# Revit family: PLCD
name_source: partatom
category: Mechanical Equipment
units: mm (PartAtom-declared; Revit-internal decimal feet)

## family parameters
Always vertical = Yes
Cut with Voids When Loaded = No
Part Type = Normal
Room Calculation Point = No
Round Connector Dimension = Use Diameter
Shared = No
Work Plane-Based = No

## types (20) — shared parameters
0 = 0' - 0"
1" = 0' - 1"
1.125" = 0' - 1 1/8"
1.5 = 0' - 1 1/2"
2" = 0' - 2"
2' = 2' - 0"
3" = 0' - 3"
4" = 0' - 4"
45 = 50.00°
FORMULA_A = 0' - 0"
FORMULA_K = 0' - 0"
Manufacturer = Loren Cook Company
Model = PLCD
ONE EIGTH = 0' - 0 1/8"
PERCENT_WIDE = 100
Type Comments = Centrifugal Plenum Fan Direct Drive Arr 4 Class 1-3
URL = www.lorencook.com
zero-valued in all types: PERCENT_A

## per-type parameters (varying)
- 120_PLCD: (C-H-H-H-H)/2=0' - 7 3/16"; (E/2)-.125"=0' - 1 11/32"; -(C - H - H - H - H) / 2=-0' - 7 3/16"; 2H=0' - 1 7/16"; A=2' - 2 5/16"; A-K-L-.125"-H-H=1' - 1 1/2"; A-L=2' - 0 1/2"; B=1' - 5 1/4"; B-E=1' - 2 5/16"; B/2=0' - 8 5/8"; C=1' - 5 1/4"; C/2=0' - 8 5/8"; D=0' - 8 5/8"; D-MOTOR_RADIUS-2"=0' - 3 5/8"; E=0' - 2 15/16"; E/2=0' - 1 15/32"; F=0' - 0 5/8"; F/2=0' - 0 5/16"; FORMULA2_A=2' - 2 5/16"; FORMULA2_K=0' - 9 7/16"; H=0' - 0 23/32"; INLET_DEPTH=0' - 3 25/32"; INLET_RAD=0' - 6 29/32"; J=1' - 4 1/4"; J-2"=-1' - 0 13/16"; K=0' - 9 7/16"; L=0' - 1 13/16"; L+K=0' - 11 1/4"; L+K+.125"=0' - 11 3/8"; L-.125"=0' - 1 11/16"; MOTOR_RADIUS=0' - 3"; MOTOR_RADIUS+1.5"=0' - 5"; MOTOR_RADIUS+2"=0' - 5"; UNIT_SIZE=120
- 135_PLCD: (C-H-H-H-H)/2=0' - 8 5/16"; (E/2)-.125"=0' - 1 15/32"; -(C - H - H - H - H) / 2=-0' - 8 5/16"; 2H=0' - 1 7/16"; A=2' - 3 5/32"; A-K-L-.125"-H-H=1' - 1 1/32"; A-L=2' - 1 3/32"; B=1' - 7 1/2"; B-E=1' - 4 5/16"; B/2=0' - 9 3/4"; C=1' - 7 1/2"; C/2=0' - 9 3/4"; D=0' - 9 3/4"; D-MOTOR_RADIUS-2"=0' - 5 3/4"; E=0' - 3 3/16"; E/2=0' - 1 19/32"; F=0' - 0 5/8"; F/2=0' - 0 5/16"; FORMULA2_A=2' - 3 5/32"; FORMULA2_K=0' - 10 1/2"; H=0' - 0 23/32"; INLET_DEPTH=0' - 4 3/16"; INLET_RAD=0' - 7 13/16"; J=1' - 3 3/4"; J-2"=-1' - 0 5/16"; K=0' - 10 1/2"; L=0' - 2 1/16"; L+K=1' - 0 9/16"; L+K+.125"=1' - 0 11/16"; L-.125"=0' - 1 15/16"; MOTOR_RADIUS=0' - 2"; MOTOR_RADIUS+1.5"=0' - 4"; MOTOR_RADIUS+2"=0' - 4"; UNIT_SIZE=135
- 150_PLCD: (C-H-H-H-H)/2=0' - 9 5/16"; (E/2)-.125"=0' - 1 15/32"; -(C - H - H - H - H) / 2=-0' - 9 5/16"; 2H=0' - 1 7/16"; A=2' - 5 27/32"; A-K-L-.125"-H-H=1' - 2 25/32"; A-L=2' - 3 25/32"; B=1' - 9 1/2"; B-E=1' - 6 5/16"; B/2=0' - 10 3/4"; C=1' - 9 1/2"; C/2=0' - 10 3/4"; D=0' - 10 3/4"; D-MOTOR_RADIUS-2"=0' - 5 1/4"; E=0' - 3 3/16"; E/2=0' - 1 19/32"; F=0' - 0 5/8"; F/2=0' - 0 5/16"; FORMULA2_A=2' - 5 27/32"; FORMULA2_K=0' - 11 7/16"; H=0' - 0 23/32"; INLET_DEPTH=0' - 4 9/16"; INLET_RAD=0' - 8 19/32"; J=1' - 5 1/2"; J-2"=-1' - 2 1/16"; K=0' - 11 7/16"; L=0' - 2 1/16"; L+K=1' - 1 1/2"; L+K+.125"=1' - 1 5/8"; L-.125"=0' - 1 15/16"; MOTOR_RADIUS=0' - 3 1/2"; MOTOR_RADIUS+1.5"=0' - 5 1/2"; MOTOR_RADIUS+2"=0' - 5 1/2"; UNIT_SIZE=150
- 165_PLCD: (C-H-H-H-H)/2=0' - 10 7/16"; (E/2)-.125"=0' - 1 15/32"; -(C - H - H - H - H) / 2=-0' - 10 7/16"; 2H=0' - 1 7/16"; A=2' - 8 7/16"; A-K-L-.125"-H-H=1' - 4 3/16"; A-L=2' - 6 3/8"; B=1' - 11 3/4"; B-E=1' - 8 9/16"; B/2=0' - 11 7/8"; C=1' - 11 3/4"; C/2=0' - 11 7/8"; D=0' - 11 7/8"; D-MOTOR_RADIUS-2"=0' - 5 7/8"; E=0' - 3 3/16"; E/2=0' - 1 19/32"; F=0' - 0 5/8"; F/2=0' - 0 5/16"; FORMULA2_A=2' - 8 7/16"; FORMULA2_K=1' - 0 5/8"; H=0' - 0 23/32"; INLET_DEPTH=0' - 5 1/16"; INLET_RAD=0' - 9 1/2"; J=1' - 6 7/8"; J-2"=-1' - 3 7/16"; K=1' - 0 5/8"; L=0' - 2 1/16"; L+K=1' - 2 11/16"; L+K+.125"=1' - 2 13/16"; L-.125"=0' - 1 15/16"; MOTOR_RADIUS=0' - 4"; MOTOR_RADIUS+1.5"=0' - 6"; MOTOR_RADIUS+2"=0' - 6"; UNIT_SIZE=165
- 180_PLCD: (C-H-H-H-H)/2=0' - 11 7/16"; (E/2)-.125"=0' - 1 31/32"; -(C - H - H - H - H) / 2=-0' - 11 7/16"; 2H=0' - 1 7/16"; A=2' - 10 17/32"; A-K-L-.125"-H-H=1' - 4 5/32"; A-L=2' - 7 15/32"; B=2' - 1 3/4"; B-E=1' - 9 9/16"; B/2=1' - 0 7/8"; C=2' - 1 3/4"; C/2=1' - 0 7/8"; D=1' - 0 7/8"; D-MOTOR_RADIUS-2"=0' - 6 7/8"; E=0' - 4 3/16"; E/2=0' - 2 3/32"; F=0' - 0 5/8"; F/2=0' - 0 5/16"; FORMULA2_A=2' - 10 17/32"; FORMULA2_K=1' - 1 3/4"; H=0' - 0 23/32"; INLET_DEPTH=0' - 5 1/2"; INLET_RAD=0' - 10 5/16"; J=1' - 6 7/8"; J-2"=-1' - 3 7/16"; K=1' - 1 3/4"; L=0' - 3 1/16"; L+K=1' - 4 13/16"; L+K+.125"=1' - 4 15/16"; L-.125"=0' - 2 15/16"; MOTOR_RADIUS=0' - 4"; MOTOR_RADIUS+1.5"=0' - 6"; MOTOR_RADIUS+2"=0' - 6"; UNIT_SIZE=180
- 195_PLCD: (C-H-H-H-H)/2=1' - 0 9/16"; (E/2)-.125"=0' - 1 31/32"; -(C - H - H - H - H) / 2=-1' - 0 9/16"; 2H=0' - 1 7/16"; A=2' - 11 21/32"; A-K-L-.125"-H-H=1' - 4 5/32"; A-L=2' - 8 19/32"; B=2' - 4"; B-E=1' - 11 13/16"; B/2=1' - 2"; C=2' - 4"; C/2=1' - 2"; D=1' - 2"; D-MOTOR_RADIUS-2"=0' - 8"; E=0' - 4 3/16"; E/2=0' - 2 3/32"; F=0' - 0 5/8"; F/2=0' - 0 5/16"; FORMULA2_A=2' - 11 21/32"; FORMULA2_K=1' - 2 7/8"; H=0' - 0 23/32"; INLET_DEPTH=0' - 5 15/16"; INLET_RAD=0' - 11 3/16"; J=1' - 6 7/8"; J-2"=-1' - 3 7/16"; K=1' - 2 7/8"; L=0' - 3 1/16"; L+K=1' - 5 15/16"; L+K+.125"=1' - 6 1/16"; L-.125"=0' - 2 15/16"; MOTOR_RADIUS=0' - 4"; MOTOR_RADIUS+1.5"=0' - 6"; MOTOR_RADIUS+2"=0' - 6"; UNIT_SIZE=195
- 210_PLCD: (C-H-H-H-H)/2=1' - 1 9/16"; (E/2)-.125"=0' - 1 31/32"; -(C - H - H - H - H) / 2=-1' - 1 9/16"; 2H=0' - 1 7/16"; A=3' - 4 3/8"; A-K-L-.125"-H-H=1' - 7 13/16"; A-L=3' - 1 5/16"; B=2' - 6"; B-E=2' - 1 13/16"; B/2=1' - 3"; C=2' - 6"; C/2=1' - 3"; D=1' - 3"; D-MOTOR_RADIUS-2"=0' - 7 13/16"; E=0' - 4 3/16"; E/2=0' - 2 3/32"; F=0' - 0 5/8"; F/2=0' - 0 5/16"; FORMULA2_A=3' - 4 3/8"; FORMULA2_K=1' - 3 15/16"; H=0' - 0 23/32"; INLET_DEPTH=0' - 6 3/8"; INLET_RAD=1' - 0"; J=1' - 10 1/2"; J-2"=-1' - 7 1/16"; K=1' - 3 15/16"; L=0' - 3 1/16"; L+K=1' - 7"; L+K+.125"=1' - 7 1/8"; L-.125"=0' - 2 15/16"; MOTOR_RADIUS=0' - 5 3/16"; MOTOR_RADIUS+1.5"=0' - 7 3/16"; MOTOR_RADIUS+2"=0' - 7 3/16"; UNIT_SIZE=210
- 225_PLCD: (C-H-H-H-H)/2=1' - 2 11/16"; (E/2)-.125"=0' - 1 31/32"; -(C - H - H - H - H) / 2=-1' - 2 11/16"; 2H=0' - 1 7/16"; A=3' - 5 3/8"; A-K-L-.125"-H-H=1' - 7 13/16"; A-L=3' - 2 5/16"; B=2' - 8 1/4"; B-E=2' - 4 1/16"; B/2=1' - 4 1/8"; C=2' - 8 1/4"; C/2=1' - 4 1/8"; D=1' - 4 1/8"; D-MOTOR_RADIUS-2"=0' - 8 15/16"; E=0' - 4 3/16"; E/2=0' - 2 3/32"; F=0' - 0 5/8"; F/2=0' - 0 5/16"; FORMULA2_A=3' - 5 3/8"; FORMULA2_K=1' - 4 15/16"; H=0' - 0 23/32"; INLET_DEPTH=0' - 6 25/32"; INLET_RAD=1' - 0 29/32"; J=1' - 10 1/2"; J-2"=-1' - 7 1/16"; K=1' - 4 15/16"; L=0' - 3 1/16"; L+K=1' - 8"; L+K+.125"=1' - 8 1/8"; L-.125"=0' - 2 15/16"; MOTOR_RADIUS=0' - 5 3/16"; MOTOR_RADIUS+1.5"=0' - 7 3/16"; MOTOR_RADIUS+2"=0' - 7 3/16"; UNIT_SIZE=225
- 245_PLCD: (C-H-H-H-H)/2=1' - 4 1/16"; (E/2)-.125"=0' - 1 31/32"; -(C - H - H - H - H) / 2=-1' - 4 1/16"; 2H=0' - 1 7/16"; A=4' - 0 1/8"; A-K-L-.125"-H-H=2' - 1 1/8"; A-L=3' - 9 1/16"; B=2' - 11"; B-E=2' - 6 13/16"; B/2=1' - 5 1/2"; C=2' - 11"; C/2=1' - 5 1/2"; D=1' - 5 1/2"; D-MOTOR_RADIUS-2"=0' - 9 3/16"; E=0' - 4 3/16"; E/2=0' - 2 3/32"; F=0' - 0 5/8"; F/2=0' - 0 5/16"; FORMULA2_A=4' - 0 1/8"; FORMULA2_K=1' - 6 3/8"; H=0' - 0 23/32"; INLET_DEPTH=0' - 7 11/32"; INLET_RAD=1' - 2"; J=2' - 3 3/4"; J-2"=-2' - 0 5/16"; K=1' - 6 3/8"; L=0' - 3 1/16"; L+K=1' - 9 7/16"; L+K+.125"=1' - 9 9/16"; L-.125"=0' - 2 15/16"; MOTOR_RADIUS=0' - 6 5/16"; MOTOR_RADIUS+1.5"=0' - 8 5/16"; MOTOR_RADIUS+2"=0' - 8 5/16"; UNIT_SIZE=245
- 270_PLCD: (C-H-H-H-H)/2=1' - 5 15/16"; (E/2)-.125"=0' - 2 7/32"; -(C - H - H - H - H) / 2=-1' - 5 15/16"; 2H=0' - 1 7/16"; A=4' - 5 5/16"; A-K-L-.125"-H-H=2' - 3 7/8"; A-L=4' - 1 3/4"; B=3' - 2 3/4"; B-E=2' - 10 1/16"; B/2=1' - 7 3/8"; C=3' - 2 3/4"; C/2=1' - 7 3/8"; D=1' - 7 3/8"; D-MOTOR_RADIUS-2"=0' - 11 1/16"; E=0' - 4 11/16"; E/2=0' - 2 11/32"; F=0' - 0 5/8"; F/2=0' - 0 5/16"; FORMULA2_A=4' - 5 5/16"; FORMULA2_K=1' - 8 5/16"; H=0' - 0 23/32"; INLET_DEPTH=0' - 8 1/8"; INLET_RAD=1' - 3 1/2"; J=2' - 6 5/8"; J-2"=-2' - 3 3/16"; K=1' - 8 5/16"; L=0' - 3 9/16"; L+K=1' - 11 7/8"; L+K+.125"=2' - 0"; L-.125"=0' - 3 7/16"; MOTOR_RADIUS=0' - 6 5/16"; MOTOR_RADIUS+1.5"=0' - 8 5/16"; MOTOR_RADIUS+2"=0' - 8 5/16"; UNIT_SIZE=270
- 300_PLCD: (C-H-H-H-H)/2=1' - 8 1/16"; (E/2)-.125"=0' - 2 7/32"; -(C - H - H - H - H) / 2=-1' - 8 1/16"; 2H=0' - 1 7/16"; A=4' - 10 13/32"; A-K-L-.125"-H-H=2' - 6 29/32"; A-L=4' - 6 27/32"; B=3' - 7"; B-E=3' - 2 5/16"; B/2=1' - 9 1/2"; C=3' - 7"; C/2=1' - 9 1/2"; D=1' - 9 1/2"; D-MOTOR_RADIUS-2"=0' - 11 11/16"; E=0' - 4 11/16"; E/2=0' - 2 11/32"; F=0' - 0 5/8"; F/2=0' - 0 5/16"; FORMULA2_A=4' - 10 13/32"; FORMULA2_K=1' - 10 3/8"; H=0' - 0 23/32"; INLET_DEPTH=0' - 8 15/16"; INLET_RAD=1' - 5 3/16"; J=2' - 9 5/8"; J-2"=-2' - 6 3/16"; K=1' - 10 3/8"; L=0' - 3 9/16"; L+K=2' - 1 15/16"; L+K+.125"=2' - 2 1/16"; L-.125"=0' - 3 7/16"; MOTOR_RADIUS=0' - 7 13/16"; MOTOR_RADIUS+1.5"=0' - 9 13/16"; MOTOR_RADIUS+2"=0' - 9 13/16"; UNIT_SIZE=300
- 330_PLCD: (C-H-H-H-H)/2=1' - 9 7/16"; (E/2)-.125"=0' - 2 23/32"; -(C - H - H - H - H) / 2=-1' - 9 7/16"; 2H=0' - 1 9/16"; A=5' - 1 27/32"; A-K-L-.125"-H-H=2' - 6 31/32"; A-L=4' - 9 9/32"; B=4' - 1 1/2"; B-E=3' - 7 13/16"; B/2=2' - 0 3/4"; C=3' - 10"; C/2=1' - 11"; D=1' - 11 5/8"; D-MOTOR_RADIUS-2"=1' - 1 13/16"; E=0' - 5 11/16"; E/2=0' - 2 27/32"; F=0' - 0 15/16"; F/2=0' - 0 15/32"; FORMULA2_A=5' - 1 27/32"; FORMULA2_K=2' - 0 5/8"; H=0' - 0 25/32"; INLET_DEPTH=0' - 9 27/32"; INLET_RAD=1' - 7 13/16"; J=2' - 9 7/8"; J-2"=-2' - 6 5/16"; K=2' - 0 5/8"; L=0' - 4 9/16"; L+K=2' - 5 3/16"; L+K+.125"=2' - 5 5/16"; L-.125"=0' - 4 7/16"; MOTOR_RADIUS=0' - 7 13/16"; MOTOR_RADIUS+1.5"=0' - 9 13/16"; MOTOR_RADIUS+2"=0' - 9 13/16"; UNIT_SIZE=330
- 365_PLCD: (C-H-H-H-H)/2=1' - 10 13/16"; (E/2)-.125"=0' - 2 23/32"; -(C - H - H - H - H) / 2=-1' - 10 13/16"; 2H=0' - 1 11/16"; A=6' - 0 19/32"; A-K-L-.125"-H-H=3' - 3 7/32"; A-L=5' - 8 1/32"; B=4' - 5 1/2"; B-E=3' - 11 13/16"; B/2=2' - 2 3/4"; C=4' - 1"; C/2=2' - 0 1/2"; D=2' - 2 1/8"; D-MOTOR_RADIUS-2"=1' - 1 7/16"; E=0' - 5 11/16"; E/2=0' - 2 27/32"; F=0' - 0 15/16"; F/2=0' - 0 15/32"; FORMULA2_A=6' - 0 19/32"; FORMULA2_K=2' - 3"; H=0' - 0 27/32"; INLET_DEPTH=0' - 10 13/16"; INLET_RAD=1' - 9 13/32"; J=3' - 6 1/8"; J-2"=-3' - 2 7/16"; K=2' - 3"; L=0' - 4 9/16"; L+K=2' - 7 9/16"; L+K+.125"=2' - 7 11/16"; L-.125"=0' - 4 7/16"; MOTOR_RADIUS=0' - 10 11/16"; MOTOR_RADIUS+1.5"=1' - 0 11/16"; MOTOR_RADIUS+2"=1' - 0 11/16"; UNIT_SIZE=365
- 402_PLCD: (C-H-H-H-H)/2=2' - 1 5/16"; (E/2)-.125"=0' - 2 31/32"; -(C - H - H - H - H) / 2=-2' - 1 5/16"; 2H=0' - 1 11/16"; A=6' - 4"; A-K-L-.125"-H-H=3' - 3 3/16"; A-L=5' - 10 7/8"; B=5' - 0"; B-E=4' - 5 13/16"; B/2=2' - 6"; C=4' - 6"; C/2=2' - 3"; D=2' - 4 3/4"; D-MOTOR_RADIUS-2"=1' - 4 1/16"; E=0' - 6 3/16"; E/2=0' - 3 3/32"; F=0' - 0 15/16"; F/2=0' - 0 15/32"; FORMULA2_A=6' - 4"; FORMULA2_K=2' - 5 7/8"; H=0' - 0 27/32"; INLET_DEPTH=0' - 11 15/16"; INLET_RAD=2' - 0"; J=3' - 6 1/8"; J-2"=-3' - 2 7/16"; K=2' - 5 7/8"; L=0' - 5 1/8"; L+K=2' - 11"; L+K+.125"=2' - 11 1/8"; L-.125"=0' - 5"; MOTOR_RADIUS=0' - 10 11/16"; MOTOR_RADIUS+1.5"=1' - 0 11/16"; MOTOR_RADIUS+2"=1' - 0 11/16"; UNIT_SIZE=402
- 445_PLCD: (C-H-H-H-H)/2=2' - 3 9/16"; (E/2)-.125"=0' - 3 15/32"; -(C - H - H - H - H) / 2=-2' - 3 9/16"; 2H=0' - 1 11/16"; A=6' - 7 31/32"; A-K-L-.125"-H-H=3' - 3 5/32"; A-L=6' - 1 27/32"; B=5' - 4"; B-E=4' - 8 13/16"; B/2=2' - 8"; C=4' - 10 1/2"; C/2=2' - 5 1/4"; D=2' - 7 7/8"; D-MOTOR_RADIUS-2"=1' - 7 3/16"; E=0' - 7 3/16"; E/2=0' - 3 19/32"; F=0' - 0 15/16"; F/2=0' - 0 15/32"; FORMULA2_A=6' - 7 31/32"; FORMULA2_K=2' - 8 7/8"; H=0' - 0 27/32"; INLET_DEPTH=1' - 1 5/32"; INLET_RAD=2' - 1 19/32"; J=3' - 6 1/8"; J-2"=-3' - 2 7/16"; K=2' - 8 7/8"; L=0' - 6 1/8"; L+K=3' - 3"; L+K+.125"=3' - 3 1/8"; L-.125"=0' - 6"; MOTOR_RADIUS=0' - 10 11/16"; MOTOR_RADIUS+1.5"=1' - 0 11/16"; MOTOR_RADIUS+2"=1' - 0 11/16"; UNIT_SIZE=445
- 490_PLCD: (C-H-H-H-H)/2=2' - 5 1/2"; (E/2)-.125"=0' - 3 23/32"; -(C - H - H - H - H) / 2=-2' - 5 1/2"; 2H=0' - 2"; A=7' - 5 11/16"; A-K-L-.125"-H-H=3' - 8 7/8"; A-L=6' - 11 1/8"; B=5' - 10"; B-E=5' - 2 5/16"; B/2=2' - 11"; C=5' - 3"; C/2=2' - 7 1/2"; D=2' - 11"; D-MOTOR_RADIUS-2"=1' - 9"; E=0' - 7 11/16"; E/2=0' - 3 27/32"; F=0' - 0 15/16"; F/2=0' - 0 15/32"; FORMULA2_A=7' - 5 11/16"; FORMULA2_K=3' - 0 1/8"; H=0' - 1"; INLET_DEPTH=1' - 2 7/16"; INLET_RAD=2' - 4"; J=4' - 0 1/8"; J-2"=-3' - 8 1/8"; K=3' - 0 1/8"; L=0' - 6 9/16"; L+K=3' - 6 11/16"; L+K+.125"=3' - 6 13/16"; L-.125"=0' - 6 7/16"; MOTOR_RADIUS=1' - 0"; MOTOR_RADIUS+1.5"=1' - 2"; MOTOR_RADIUS+2"=1' - 2"; UNIT_SIZE=490
- 540_PLCD: (C-H-H-H-H)/2=2' - 8 1/2"; (E/2)-.125"=0' - 3 3/4"; -(C - H - H - H - H) / 2=-2' - 8 1/2"; 2H=0' - 2"; A=7' - 9 3/8"; A-K-L-.125"-H-H=3' - 8 7/8"; A-L=7' - 2 3/4"; B=6' - 3"; B-E=5' - 7 9/32"; B/2=3' - 1 1/2"; C=5' - 9"; C/2=2' - 10 1/2"; D=3' - 2 5/8"; D-MOTOR_RADIUS-2"=2' - 0 5/8"; E=0' - 7 23/32"; E/2=0' - 3 7/8"; F=0' - 1 1/16"; F/2=0' - 0 17/32"; FORMULA2_A=7' - 9 3/8"; FORMULA2_K=3' - 3 3/4"; H=0' - 1"; INLET_DEPTH=1' - 3 29/32"; INLET_RAD=2' - 6"; J=4' - 0 1/8"; J-2"=-3' - 8 1/8"; K=3' - 3 3/4"; L=0' - 6 5/8"; L+K=3' - 10 3/8"; L+K+.125"=3' - 10 1/2"; L-.125"=0' - 6 1/2"; MOTOR_RADIUS=1' - 0"; MOTOR_RADIUS+1.5"=1' - 2"; MOTOR_RADIUS+2"=1' - 2"; UNIT_SIZE=540
- 600_PLCD: (C-H-H-H-H)/2=2' - 11 1/2"; (E/2)-.125"=0' - 4"; -(C - H - H - H - H) / 2=-2' - 11 1/2"; 2H=0' - 2"; A=8' - 2 1/4"; A-K-L-.125"-H-H=3' - 8 7/8"; A-L=7' - 7 1/8"; B=6' - 10"; B-E=6' - 1 25/32"; B/2=3' - 5"; C=6' - 3"; C/2=3' - 1 1/2"; D=3' - 6 7/8"; D-MOTOR_RADIUS-2"=2' - 4 7/8"; E=0' - 8 7/32"; E/2=0' - 4 1/8"; F=0' - 1 1/16"; F/2=0' - 0 17/32"; FORMULA2_A=8' - 2 1/4"; FORMULA2_K=3' - 8 1/8"; H=0' - 1"; INLET_DEPTH=1' - 5 21/32"; INLET_RAD=2' - 8 13/16"; J=4' - 0 1/8"; J-2"=-3' - 8 1/8"; K=3' - 8 1/8"; L=0' - 7 1/8"; L+K=4' - 3 1/4"; L+K+.125"=4' - 3 3/8"; L-.125"=0' - 7"; MOTOR_RADIUS=1' - 0"; MOTOR_RADIUS+1.5"=1' - 2"; MOTOR_RADIUS+2"=1' - 2"; UNIT_SIZE=600
- 660_PLCD: (C-H-H-H-H)/2=3' - 3 1/4"; (E/2)-.125"=0' - 4 1/2"; -(C - H - H - H - H) / 2=-3' - 3 1/4"; 2H=0' - 1 3/4"; A=8' - 8 3/8"; A-K-L-.125"-H-H=3' - 9 13/16"; A-L=8' - 0 1/4"; B=7' - 6"; B-E=6' - 8 25/32"; B/2=3' - 9"; C=6' - 10"; C/2=3' - 5"; D=3' - 11 1/4"; D-MOTOR_RADIUS-2"=2' - 9 1/4"; E=0' - 9 7/32"; E/2=0' - 4 5/8"; F=0' - 1 1/16"; F/2=0' - 0 17/32"; FORMULA2_A=8' - 8 3/8"; FORMULA2_K=4' - 0 9/16"; H=0' - 0 7/8"; INLET_DEPTH=1' - 7 7/16"; INLET_RAD=3' - 0"; J=4' - 0 7/8"; J-2"=-3' - 9 1/8"; K=4' - 0 9/16"; L=0' - 8 1/8"; L+K=4' - 8 11/16"; L+K+.125"=4' - 8 13/16"; L-.125"=0' - 8"; MOTOR_RADIUS=1' - 0"; MOTOR_RADIUS+1.5"=1' - 2"; MOTOR_RADIUS+2"=1' - 2"; UNIT_SIZE=660
- 730_PLCD: (C-H-H-H-H)/2=3' - 8 1/4"; (E/2)-.125"=0' - 4 1/2"; -(C - H - H - H - H) / 2=-3' - 8 1/4"; 2H=0' - 1 3/4"; A=11' - 3 7/8"; A-K-L-.125"-H-H=6' - 0 5/16"; A-L=10' - 7 3/4"; B=7' - 8"; B-E=6' - 10 25/32"; B/2=3' - 10"; C=7' - 8"; C/2=3' - 10"; D=4' - 4 1/4"; D-MOTOR_RADIUS-2"=3' - 0 1/4"; E=0' - 9 7/32"; E/2=0' - 4 5/8"; F=0' - 1 1/16"; F/2=0' - 0 17/32"; FORMULA2_A=11' - 3 7/8"; FORMULA2_K=4' - 5 9/16"; H=0' - 0 7/8"; INLET_DEPTH=1' - 9 7/16"; INLET_RAD=3' - 0 13/16"; J=6' - 3 3/8"; J-2"=-5' - 11 5/8"; K=4' - 5 9/16"; L=0' - 8 1/8"; L+K=5' - 1 11/16"; L+K+.125"=5' - 1 13/16"; L-.125"=0' - 8"; MOTOR_RADIUS=1' - 2"; MOTOR_RADIUS+1.5"=1' - 4"; MOTOR_RADIUS+2"=1' - 4"; UNIT_SIZE=730

## geometry (parser evidence)
native form markers: Sweep x1
no freeform markers — native parametric forms only
